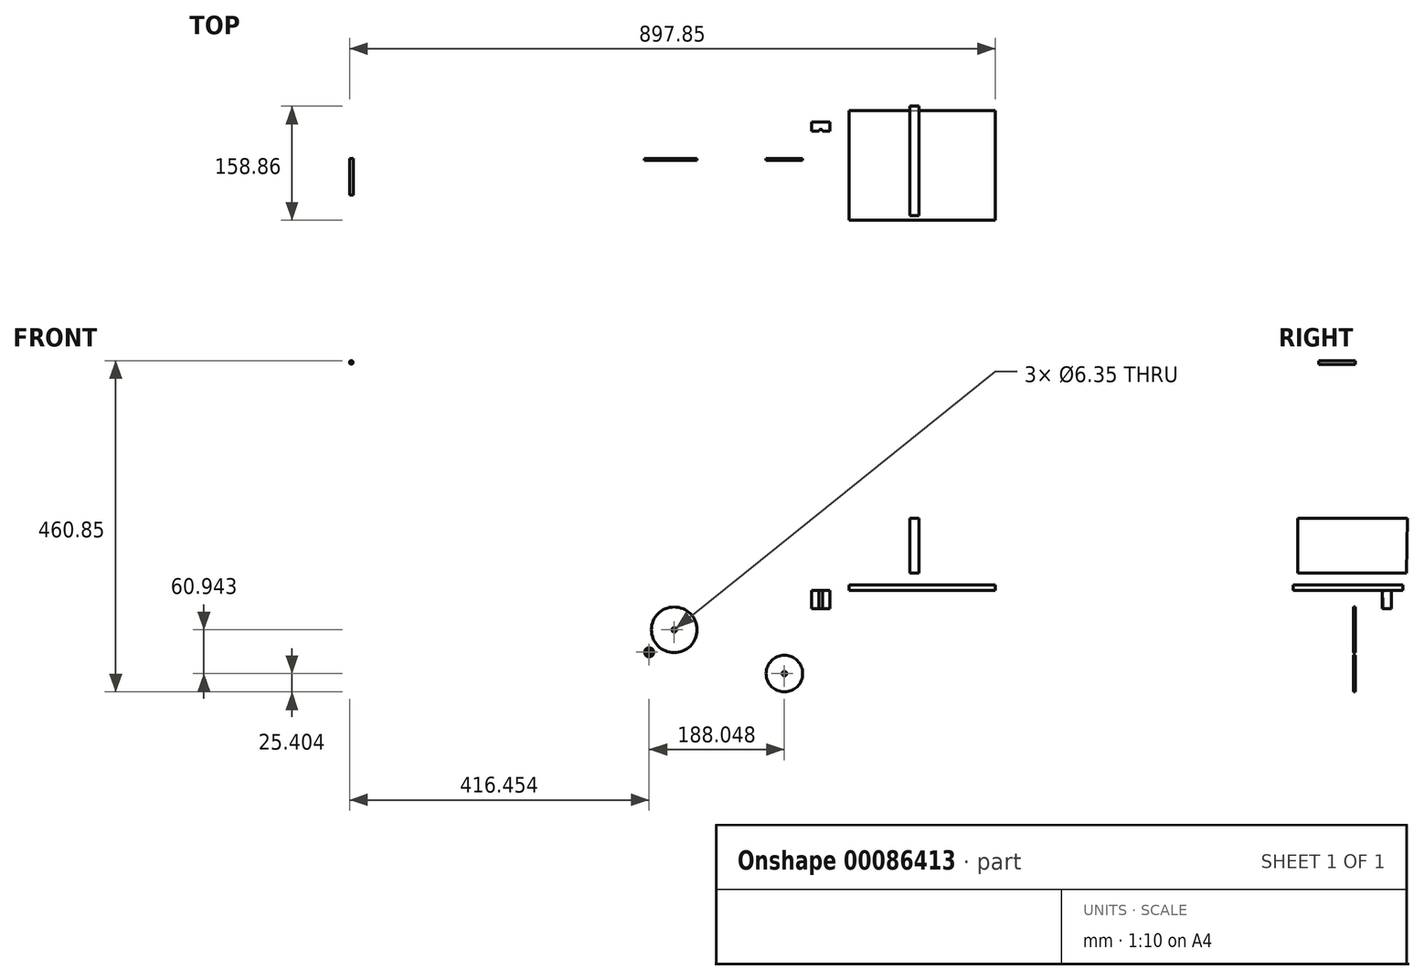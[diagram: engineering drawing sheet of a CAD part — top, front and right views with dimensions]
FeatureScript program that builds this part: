
annotation { "Feature Type Name" : "Feature", "Feature Type Description" : "" }
export const myFeature = defineFeature(function(context is Context, id is Id, definition is map)
    precondition{}
    {
        {
            var Q0;
            Q0=qCreatedBy(makeId("Top.planeOp"),FACE);
            var sketch = newSketch(context, id + "F0", { "sketchPlane" : qUnion([Q0])});
            skLineSegment(sketch, "E0.bottom", {"start": v(-84.08, 66.15) * mm, "end": v(119.12, 66.15) * mm});
            skLineSegment(sketch, "E0.top", {"start": v(-84.08, -86.25) * mm, "end": v(119.12, -86.25) * mm});
            skLineSegment(sketch, "E0.left", {"start": v(-84.08, 66.15) * mm, "end": v(-84.08, -86.25) * mm});
            skLineSegment(sketch, "E0.right", {"start": v(119.12, 66.15) * mm, "end": v(119.12, -86.25) * mm});
            skSolve(sketch);
        }
        {
            var Q0;
            Q0=makeQuery(id+"F0.imprint","IMPRINT",FACE,{"disambiguationData":[TD([[makeQuery(id+"F0.imprint","IMPRINT",EDGE,{"derivedFrom":sQuery(id+"F0.wireOp",EDGE,"E0.bottom")}),-1.0]])]});
            extrude(context, id + "F1", {"entities" : qUnion([Q0]), "depth" : 7.62 * mm});
        }
        {
            var Q0;
            Q0=qCreatedBy(makeId("Right.planeOp"),FACE);
            var sketch = newSketch(context, id + "F2", { "sketchPlane" : qUnion([Q0])});
            skLineSegment(sketch, "E1", {"start": v(72.6, 100.52) * mm, "end": v(-79.8, 100.52) * mm});
            skLineSegment(sketch, "E2", {"start": v(-79.8, 100.52) * mm, "end": v(-79.8, 24.32) * mm});
            skLineSegment(sketch, "E3", {"start": v(-79.8, 24.32) * mm, "end": v(71.62, 24.32) * mm});
            skLineSegment(sketch, "E4", {"start": v(71.62, 24.32) * mm, "end": v(72.6, 100.52) * mm});
            skSolve(sketch);
        }
        {
            var Q0;
            Q0=makeQuery(id+"F2.imprint","IMPRINT",FACE,{"disambiguationData":[TD([[makeQuery(id+"F2.imprint","IMPRINT",EDGE,{"derivedFrom":sQuery(id+"F2.wireOp",EDGE,"E1")}),1.0]])]});
            extrude(context, id + "F3", {"entities" : qUnion([Q0]), "depth" : 12.7 * mm});
        }
        {
            var Q0;
            Q0=qCreatedBy(makeId("Top.planeOp"),FACE);
            var sketch = newSketch(context, id + "F4", { "sketchPlane" : qUnion([Q0])});
            skLineSegment(sketch, "E5.bottom", {"start": v(-136.34, 50.57) * mm, "end": v(-110.94, 50.57) * mm});
            skLineSegment(sketch, "E5.top", {"start": v(-136.34, 25.17) * mm, "end": v(-110.94, 25.17) * mm});
            skLineSegment(sketch, "E5.left", {"start": v(-136.34, 50.57) * mm, "end": v(-136.34, 25.17) * mm});
            skLineSegment(sketch, "E5.right", {"start": v(-110.94, 50.57) * mm, "end": v(-110.94, 25.17) * mm});
            skLineSegment(sketch, "E6", {"start": v(-136.34, 37.87) * mm, "end": v(-110.94, 37.87) * mm});
            skLineSegment(sketch, "E7", {"start": v(-123.64, 25.17) * mm, "end": v(-123.64, 50.57) * mm});
            skCircle(sketch, "E8", {"center": v(-123.64, 37.87) * mm, "radius": 2.54 * mm});
            skSolve(sketch);
        }
        {
            var Q0;
            Q0=makeQuery(id+"F4.imprint","IMPRINT",FACE,{"disambiguationData":[TD([[makeQuery(id+"F4.imprint","IMPRINT",EDGE,{"derivedFrom":sQuery(id+"F4.wireOp",EDGE,"E5.bottom")}),-1.0]])]});
            extrude(context, id + "F5", {"entities" : qUnion([Q0]), "oppositeDirection" : true, "depth" : 25.4 * mm});
        }
        {
            var Q0;
            Q0=qCreatedBy(makeId("Front.planeOp"),FACE);
            var sketch = newSketch(context, id + "F6", { "sketchPlane" : qUnion([Q0])});
            skCircle(sketch, "E9", {"center": v(-776.2, 317.08) * mm, "radius": 2.54 * mm});
            skSolve(sketch);
        }
        {
            var Q0;
            Q0=makeQuery(id+"F6.imprint","IMPRINT",FACE,{"disambiguationData":[TD([[makeQuery(id+"F6.imprint","IMPRINT",EDGE,{"derivedFrom":sQuery(id+"F6.wireOp",EDGE,"E9")}),1.0]])]});
            extrude(context, id + "F7", {"entities" : qUnion([Q0]), "depth" : 50.8 * mm});
        }
        {
            var Q0;
            Q0=qCreatedBy(makeId("Front.planeOp"),FACE);
            var sketch = newSketch(context, id + "F8", { "sketchPlane" : qUnion([Q0])});
            skCircle(sketch, "E10", {"center": v(-362.28, -86.1) * mm, "radius": 6.35 * mm});
            skCircle(sketch, "E11", {"center": v(-327.4, -54.88) * mm, "radius": 31.75 * mm});
            skCircle(sketch, "E12", {"center": v(-174.23, -115.83) * mm, "radius": 25.4 * mm});
            skSolve(sketch);
        }
        {
            var Q0;
            Q0=makeQuery(id+"F8.imprint","IMPRINT",FACE,{"disambiguationData":[TD([[makeQuery(id+"F8.imprint","IMPRINT",EDGE,{"derivedFrom":sQuery(id+"F8.wireOp",EDGE,"E11")}),1.0]])]});
            var Q1;
            Q1=makeQuery(id+"F8.imprint","IMPRINT",FACE,{"disambiguationData":[TD([[makeQuery(id+"F8.imprint","IMPRINT",EDGE,{"derivedFrom":sQuery(id+"F8.wireOp",EDGE,"E10")}),1.0]])]});
            var Q2;
            Q2=makeQuery(id+"F8.imprint","IMPRINT",FACE,{"disambiguationData":[TD([[makeQuery(id+"F8.imprint","IMPRINT",EDGE,{"derivedFrom":sQuery(id+"F8.wireOp",EDGE,"E12")}),1.0]])]});
            extrude(context, id + "F9", {"entities" : qUnion([Q0, Q1, Q2]), "depth" : 2.54 * mm});
        }
        {
            var Q0;
            Q0=makeQuery(id+"F9.opExtrude","CAP_FACE",FACE,{"disambiguationData":[OSD([sQuery(id+"F8.wireOp",EDGE,"E11")])],"isStart":false});
            var sketch = newSketch(context, id + "F10", { "sketchPlane" : qUnion([Q0])});
            skCircle(sketch, "E13", {"center": v(-327.4, -54.88) * mm, "radius": 2.54 * mm});
            skSolve(sketch);
        }
        {
            var Q0;
            Q0=sQuery(id+"F10.wireOp",VERTEX,"E13.center");
            var Q1;
            Q1=makeQuery(id+"F9.opExtrude","SWEPT_BODY",BODY,{"disambiguationData":[OSD([sQuery(id+"F8.wireOp",EDGE,"E11")])]});
            hole(context, id + "F11", {"style" : HoleStyle.SIMPLE, "endStyle" : HoleEndStyle.THROUGH, "holeDiameter" : 6.35 * mm, "locations" : qUnion([Q0]), "scope" : qUnion([Q1]), "isTappedThrough" : true});
        }
        {
            var Q0;
            Q0=makeQuery(id+"F9.opExtrude","CAP_FACE",FACE,{"disambiguationData":[OSD([sQuery(id+"F8.wireOp",EDGE,"E10")])],"isStart":false});
            var sketch = newSketch(context, id + "F12", { "sketchPlane" : qUnion([Q0])});
            skCircle(sketch, "E14", {"center": v(-362.28, -86.1) * mm, "radius": 2.54 * mm});
            skSolve(sketch);
        }
        {
            var Q0;
            Q0=sQuery(id+"F12.wireOp",VERTEX,"E14.center");
            var Q1;
            Q1=makeQuery(id+"F9.opExtrude","SWEPT_BODY",BODY,{"disambiguationData":[OSD([sQuery(id+"F8.wireOp",EDGE,"E10")])]});
            hole(context, id + "F13", {"style" : HoleStyle.SIMPLE, "endStyle" : HoleEndStyle.THROUGH, "holeDiameter" : 6.35 * mm, "locations" : qUnion([Q0]), "scope" : qUnion([Q1]), "isTappedThrough" : true});
        }
        {
            var Q0;
            Q0=makeQuery(id+"F9.opExtrude","CAP_FACE",FACE,{"disambiguationData":[OSD([sQuery(id+"F8.wireOp",EDGE,"E12")])],"isStart":false});
            var sketch = newSketch(context, id + "F14", { "sketchPlane" : qUnion([Q0])});
            skCircle(sketch, "E15", {"center": v(-174.23, -115.83) * mm, "radius": 2.54 * mm});
            skSolve(sketch);
        }
        {
            var Q0;
            Q0=sQuery(id+"F14.wireOp",VERTEX,"E15.center");
            var Q1;
            Q1=makeQuery(id+"F9.opExtrude","SWEPT_BODY",BODY,{"disambiguationData":[OSD([sQuery(id+"F8.wireOp",EDGE,"E12")])]});
            hole(context, id + "F15", {"style" : HoleStyle.SIMPLE, "endStyle" : HoleEndStyle.THROUGH, "holeDiameter" : 6.35 * mm, "locations" : qUnion([Q0]), "scope" : qUnion([Q1]), "isTappedThrough" : true});
        }
    });
